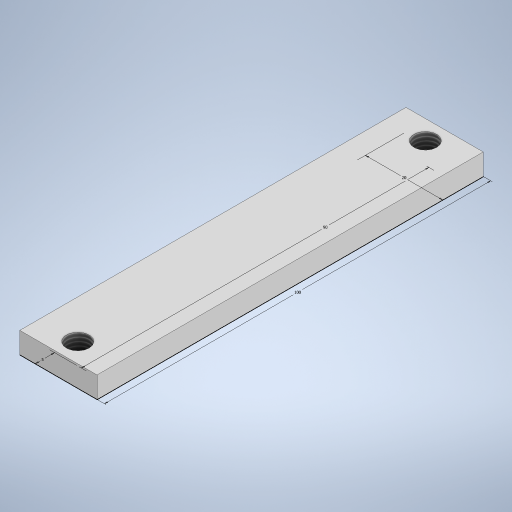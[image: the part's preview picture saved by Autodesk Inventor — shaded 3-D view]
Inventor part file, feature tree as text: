
AUTODESK INVENTOR PART (.ipt)
format: ipt  version: 2023 (Build 270158000, 158)  size: 242,688 bytes
history: native  units: mm
features: sketch x1, extrude x1, hole x1
ambient origin geometry x8: Origin, YZ Plane, XZ Plane, XY Plane, X Axis, Y Axis, Z Axis, Center Point
bodies: Solid1 (feature_tree)
feature tree (3):
  sketch  "Sketch1"  dims[d0=100.0mm d1=20.0mm d2=90.0mm d3=5.0mm d4=5.5mm d5=0.0mm d6=5.917468mm d7=14.0mm d8=4.0mm d9=2.0mm d10=90.0deg d11=19.1mm d12=20.594885mm]
  extrude  "Extrusion1"  Depth=20.0mm
  hole  "Hole1"  [1 undecoded]
note: 1 required parameter value undecoded (feature->parameter linkage not recoverable at this tier; creation-order binding heuristic only, values carry confidence <= 0.55)
